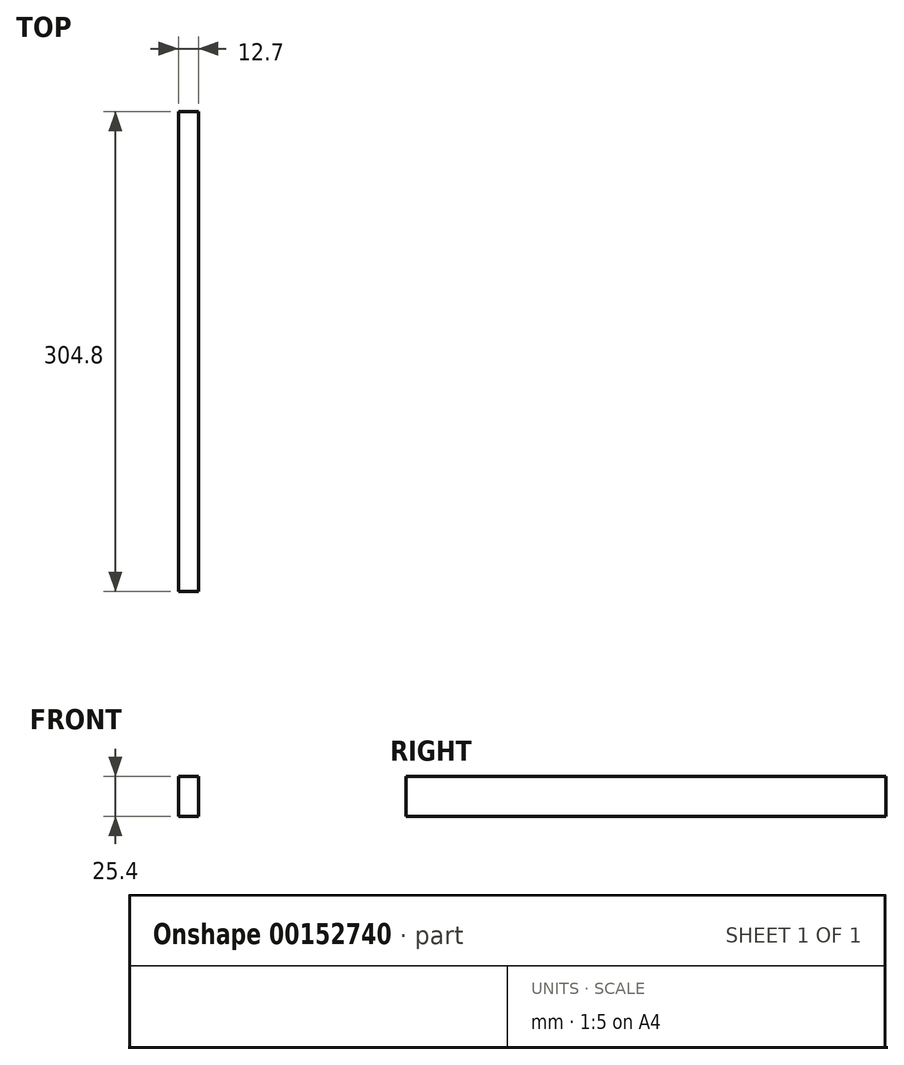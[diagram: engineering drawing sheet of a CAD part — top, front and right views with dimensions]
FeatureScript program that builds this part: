
annotation { "Feature Type Name" : "Feature", "Feature Type Description" : "" }
export const myFeature = defineFeature(function(context is Context, id is Id, definition is map)
    precondition{}
    {
        {
            var Q0;
            Q0=qCreatedBy(makeId("Top.planeOp"),FACE);
            var sketch = newSketch(context, id + "F0", { "sketchPlane" : qUnion([Q0])});
            skLineSegment(sketch, "E0.bottom", {"start": v(0, 0) * mm, "end": v(12.7, 0) * mm});
            skLineSegment(sketch, "E0.top", {"start": v(0, 304.8) * mm, "end": v(12.7, 304.8) * mm});
            skLineSegment(sketch, "E0.left", {"start": v(0, 0) * mm, "end": v(0, 304.8) * mm});
            skLineSegment(sketch, "E0.right", {"start": v(12.7, 0) * mm, "end": v(12.7, 304.8) * mm});
            skSolve(sketch);
        }
        {
            var Q0;
            Q0 = qSketchRegion(id + "F0", true);
            extrude(context, id + "F1", {"entities" : qUnion([Q0]), "depth" : 25.4 * mm});
        }
    });
